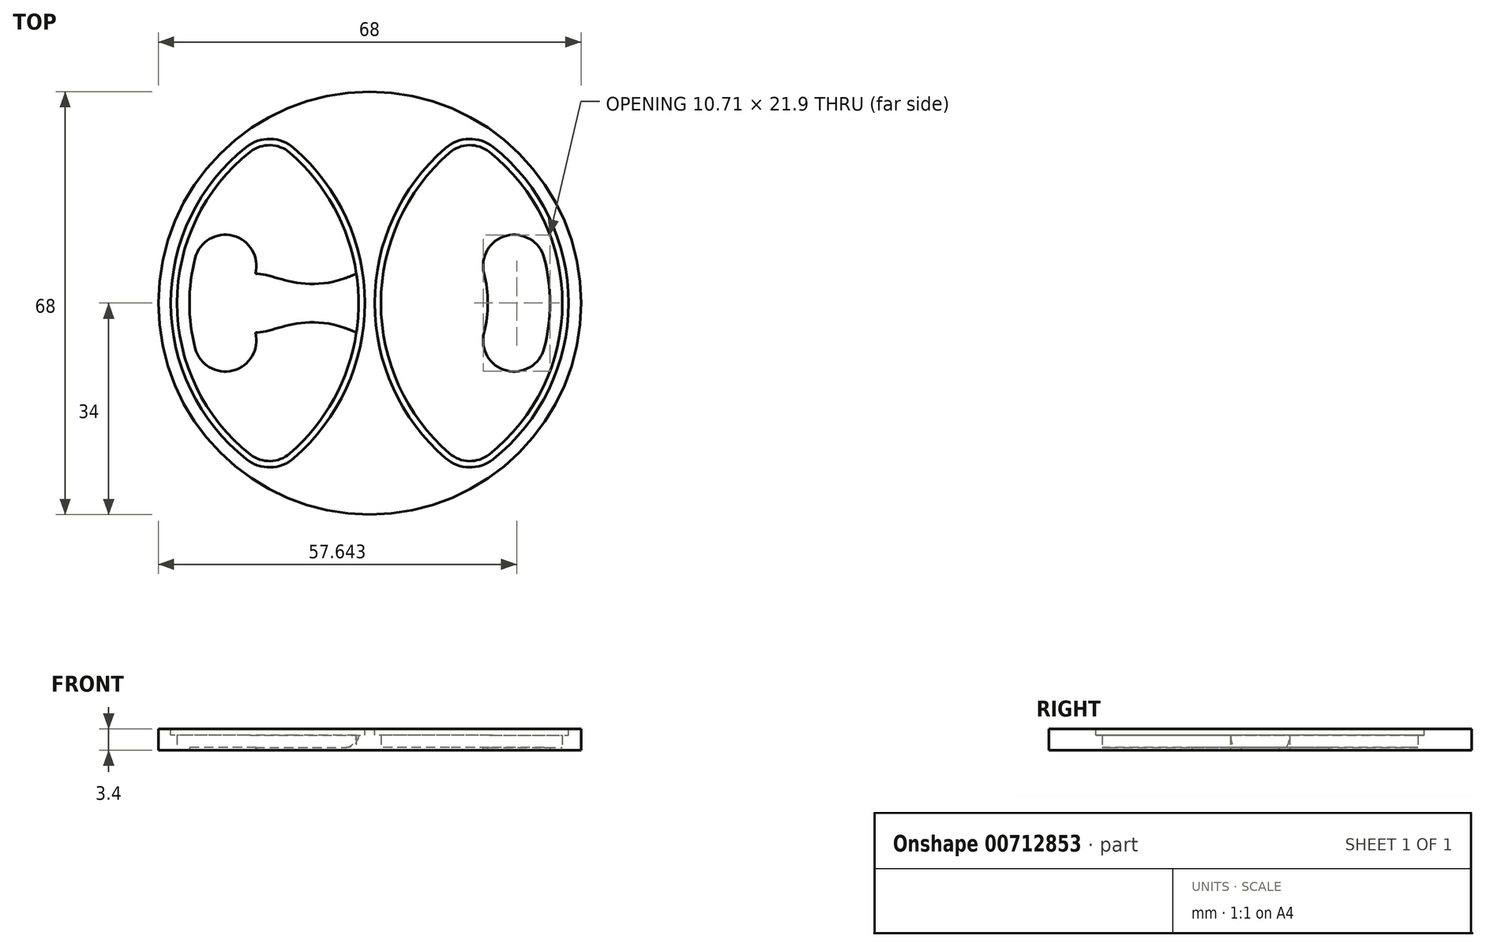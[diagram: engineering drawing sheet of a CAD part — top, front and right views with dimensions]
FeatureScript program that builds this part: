
annotation { "Feature Type Name" : "Feature", "Feature Type Description" : "" }
export const myFeature = defineFeature(function(context is Context, id is Id, definition is map)
    precondition{}
    {
        {
            var Q0;
            Q0=qCreatedBy(makeId("Top.planeOp"),FACE);
            var sketch = newSketch(context, id + "F0", { "sketchPlane" : qUnion([Q0])});
            skCircle(sketch, "E0", {"center": v(0, 0) * mm, "radius": 34 * mm});
            skArc(sketch, "E1", {"start": v(-18.4, 4.75) * mm, "mid": v(-21.99, 10.84) * mm, "end": v(-28.08, 7.25) * mm});
            skArc(sketch, "E2.MirrorC", {"start": v(-18.4, -4.75) * mm, "mid": v(-21.99, -10.84) * mm, "end": v(-28.08, -7.25) * mm});
            skArc(sketch, "E3", {"start": v(-28.08, 7.25) * mm, "mid": v(-29, 0) * mm, "end": v(-28.08, -7.25) * mm});
            skArc(sketch, "E4", {"start": v(-18.4, 4.75) * mm, "mid": v(-19, 0) * mm, "end": v(-18.4, -4.75) * mm});
            skArc(sketch, "E5", {"start": v(-19.22, 24.33) * mm, "mid": v(-31, 0) * mm, "end": v(-19.22, -24.33) * mm});
            skArc(sketch, "E6.MirrorCS", {"start": v(18.4, 4.75) * mm, "mid": v(19, 0) * mm, "end": v(18.4, -4.75) * mm});
            skArc(sketch, "E7.MirrorCS", {"start": v(28.08, 7.25) * mm, "mid": v(29, 0) * mm, "end": v(28.08, -7.25) * mm});
            skArc(sketch, "E8.MirrorCS", {"start": v(18.4, 4.75) * mm, "mid": v(21.99, 10.84) * mm, "end": v(28.08, 7.25) * mm});
            skArc(sketch, "E9.MirrorCS", {"start": v(18.4, -4.75) * mm, "mid": v(21.99, -10.84) * mm, "end": v(28.08, -7.25) * mm});
            skPoint(sketch, "E10", {"position": v(19, 0) * mm});
            skArc(sketch, "E11", {"start": v(-12.84, -24.18) * mm, "mid": v(-1.8, 0) * mm, "end": v(-12.84, 24.18) * mm});
            skPoint(sketch, "E12.visualSharp", {"position": v(-15.97, 26.57) * mm});
            skArc(sketch, "E12.filletArc", {"start": v(-12.84, 24.18) * mm, "mid": v(-16, 25.4) * mm, "end": v(-19.22, 24.33) * mm});
            skPoint(sketch, "E13.visualSharp", {"position": v(-15.97, -26.57) * mm});
            skArc(sketch, "E13.filletArc", {"start": v(-19.22, -24.33) * mm, "mid": v(-16, -25.4) * mm, "end": v(-12.84, -24.18) * mm});
            skFitSpline(sketch, "E14", {"points": [v(-18.4, 4.75) * mm, v(-2.15, 4.75) * mm], "startDerivative": vector(9.76, 0) * mm, "endDerivative": vector(23.54, 11.25) * mm});
            skFitSpline(sketch, "E15.MirrorCS", {"points": [v(-18.4, -4.75) * mm, v(-2.15, -4.75) * mm], "startDerivative": vector(9.76, 0) * mm, "endDerivative": vector(23.54, -11.25) * mm});
            skArc(sketch, "E16", {"start": v(-21.5, 10.68) * mm, "mid": v(-24, 0) * mm, "end": v(-21.5, -10.68) * mm, "construction": true});
            skSolve(sketch);
        }
        {
            var Q0;
            Q0=makeQuery(id+"F0.imprint","IMPRINT",FACE,{"disambiguationData":[TD([[makeQuery(id+"F0.imprint","IMPRINT",EDGE,{"derivedFrom":sQuery(id+"F0.wireOp",EDGE,"E0")}),1.0]])]});
            var Q1;
            Q1=makeQuery(id+"F0.imprint","IMPRINT",FACE,{"disambiguationData":[TD([[makeQuery(id+"F0.imprint","IMPRINT",EDGE,{"derivedFrom":sQuery(id+"F0.wireOp",EDGE,"E1")}),1.0]])]});
            var Q2;
            Q2=makeQuery(id+"F0.imprint","IMPRINT",FACE,{"disambiguationData":[TD([[makeQuery(id+"F0.imprint","IMPRINT",EDGE,{"derivedFrom":sQuery(id+"F0.wireOp",EDGE,"E4")}),1.0]])]});
            extrude(context, id + "F1", {"entities" : qUnion([Q0, Q1, Q2]), "depth" : 0.4 * mm, "offsetDistance" : 25 * mm});
        }
        {
            var Q0;
            Q0=makeQuery(id+"F1.opExtrude","CAP_FACE",FACE,{"disambiguationData":[OSD([sQuery(id+"F0.wireOp",EDGE,"E0"),sQuery(id+"F0.wireOp",EDGE,"E1"),sQuery(id+"F0.wireOp",EDGE,"E2.MirrorC"),sQuery(id+"F0.wireOp",EDGE,"E3"),sQuery(id+"F0.wireOp",EDGE,"E5"),sQuery(id+"F0.wireOp",EDGE,"E6.MirrorCS"),sQuery(id+"F0.wireOp",EDGE,"E7.MirrorCS"),sQuery(id+"F0.wireOp",EDGE,"E8.MirrorCS"),sQuery(id+"F0.wireOp",EDGE,"E9.MirrorCS"),sQuery(id+"F0.wireOp",EDGE,"E11"),sQuery(id+"F0.wireOp",EDGE,"E12.filletArc"),sQuery(id+"F0.wireOp",EDGE,"E13.filletArc"),sQuery(id+"F0.wireOp",EDGE,"E14"),sQuery(id+"F0.wireOp",EDGE,"E15.MirrorCS")])],"isStart":false});
            var sketch = newSketch(context, id + "F2", { "sketchPlane" : qUnion([Q0])});
            skCircle(sketch, "E17.0", {"center": v(0, 0) * mm, "radius": 34 * mm});
            skArc(sketch, "E18.0", {"start": v(-19.22, 24.33) * mm, "mid": v(-31, 0) * mm, "end": v(-19.22, -24.33) * mm});
            skArc(sketch, "E19.0", {"start": v(-12.84, -24.18) * mm, "mid": v(-1.8, 0) * mm, "end": v(-12.84, 24.18) * mm});
            skArc(sketch, "E20.0", {"start": v(-12.84, 24.18) * mm, "mid": v(-16, 25.4) * mm, "end": v(-19.22, 24.33) * mm});
            skArc(sketch, "E21.0", {"start": v(-19.22, -24.33) * mm, "mid": v(-16, -25.4) * mm, "end": v(-12.84, -24.18) * mm});
            skArc(sketch, "E22.MirrorCS", {"start": v(12.84, 24.18) * mm, "mid": v(16, 25.4) * mm, "end": v(19.22, 24.33) * mm});
            skArc(sketch, "E23.MirrorCS", {"start": v(12.84, -24.18) * mm, "mid": v(1.8, 0) * mm, "end": v(12.84, 24.18) * mm});
            skArc(sketch, "E24.MirrorCS", {"start": v(19.22, 24.33) * mm, "mid": v(31, 0) * mm, "end": v(19.22, -24.33) * mm});
            skArc(sketch, "E25.MirrorCS", {"start": v(19.22, -24.33) * mm, "mid": v(16, -25.4) * mm, "end": v(12.84, -24.18) * mm});
            skSolve(sketch);
        }
        {
            var Q0;
            Q0 = qSketchRegion(id + "F2", true);
            extrude(context, id + "F3", {"entities" : qUnion([Q0]), "operationType" : NewBodyOperationType.ADD, "depth" : 3 * mm, "offsetDistance" : 25 * mm});
        }
        {
            var Q0;
            Q0=makeQuery(id+"F3.opExtrude","CAP_FACE",FACE,{"disambiguationData":[OSD([sQuery(id+"F2.wireOp",EDGE,"E17.0"),sQuery(id+"F2.wireOp",EDGE,"E18.0"),sQuery(id+"F2.wireOp",EDGE,"E19.0"),sQuery(id+"F2.wireOp",EDGE,"E20.0"),sQuery(id+"F2.wireOp",EDGE,"E21.0"),sQuery(id+"F2.wireOp",EDGE,"E22.MirrorCS"),sQuery(id+"F2.wireOp",EDGE,"E24.MirrorCS"),sQuery(id+"F2.wireOp",EDGE,"E25.MirrorCS"),sQuery(id+"F2.wireOp",EDGE,"E23.MirrorCS")])],"isStart":false});
            var sketch = newSketch(context, id + "F4", { "sketchPlane" : qUnion([Q0])});
            skArc(sketch, "E26.0", {"start": v(-19.22, 24.33) * mm, "mid": v(-31, 0) * mm, "end": v(-19.22, -24.33) * mm});
            skArc(sketch, "E27.0", {"start": v(-12.84, 24.18) * mm, "mid": v(-16, 25.4) * mm, "end": v(-19.22, 24.33) * mm});
            skArc(sketch, "E28.0", {"start": v(-12.84, -24.18) * mm, "mid": v(-1.8, 0) * mm, "end": v(-12.84, 24.18) * mm});
            skArc(sketch, "E29.0", {"start": v(-19.22, -24.33) * mm, "mid": v(-16, -25.4) * mm, "end": v(-12.84, -24.18) * mm});
            skArc(sketch, "E30.0", {"start": v(-19.84, 25.11) * mm, "mid": v(-32, 0) * mm, "end": v(-19.84, -25.11) * mm});
            skArc(sketch, "E30.1", {"start": v(-12.19, 24.94) * mm, "mid": v(-15.98, 26.4) * mm, "end": v(-19.84, 25.11) * mm});
            skArc(sketch, "E30.2", {"start": v(-12.19, -24.94) * mm, "mid": v(-0.8, 0) * mm, "end": v(-12.19, 24.94) * mm});
            skArc(sketch, "E30.3", {"start": v(-19.84, -25.11) * mm, "mid": v(-15.98, -26.4) * mm, "end": v(-12.19, -24.94) * mm});
            skArc(sketch, "E31.MirrorCS", {"start": v(12.19, 24.94) * mm, "mid": v(15.98, 26.4) * mm, "end": v(19.84, 25.11) * mm});
            skArc(sketch, "E32.MirrorCS", {"start": v(12.84, 24.18) * mm, "mid": v(16, 25.4) * mm, "end": v(19.22, 24.33) * mm});
            skArc(sketch, "E33.MirrorCS", {"start": v(12.19, -24.94) * mm, "mid": v(0.8, 0) * mm, "end": v(12.19, 24.94) * mm});
            skArc(sketch, "E34.MirrorCS", {"start": v(12.84, -24.18) * mm, "mid": v(1.8, 0) * mm, "end": v(12.84, 24.18) * mm});
            skArc(sketch, "E35.MirrorCS", {"start": v(19.84, -25.11) * mm, "mid": v(15.98, -26.4) * mm, "end": v(12.19, -24.94) * mm});
            skArc(sketch, "E36.MirrorCS", {"start": v(19.22, -24.33) * mm, "mid": v(16, -25.4) * mm, "end": v(12.84, -24.18) * mm});
            skArc(sketch, "E37.MirrorCS", {"start": v(19.22, 24.33) * mm, "mid": v(31, 0) * mm, "end": v(19.22, -24.33) * mm});
            skArc(sketch, "E38.MirrorCS", {"start": v(19.84, 25.11) * mm, "mid": v(32, 0) * mm, "end": v(19.84, -25.11) * mm});
            skSolve(sketch);
        }
        {
            var Q0;
            Q0 = qSketchRegion(id + "F4", true);
            extrude(context, id + "F5", {"entities" : qUnion([Q0]), "operationType" : NewBodyOperationType.REMOVE, "oppositeDirection" : true, "depth" : 1 * mm, "offsetDistance" : 25 * mm});
        }
        {
            var Q0;
            Q0=makeQuery(id+"F3.opExtrude","CAP_EDGE",EDGE,{"disambiguationData":[OSD([sQuery(id+"F2.wireOp",EDGE,"E19.0")])],"isStart":true});
            var Q1;
            Q1=makeQuery(id+"F3.opExtrude","CAP_EDGE",EDGE,{"disambiguationData":[OSD([sQuery(id+"F2.wireOp",EDGE,"E23.MirrorCS")])],"isStart":true});
            fillet(context, id + "F6", {"entities" : qUnion([Q0, Q1]), "radius" : 2 * mm, "tangentPropagation" : true, "allowEdgeOverflow" : false});
        }
    });
